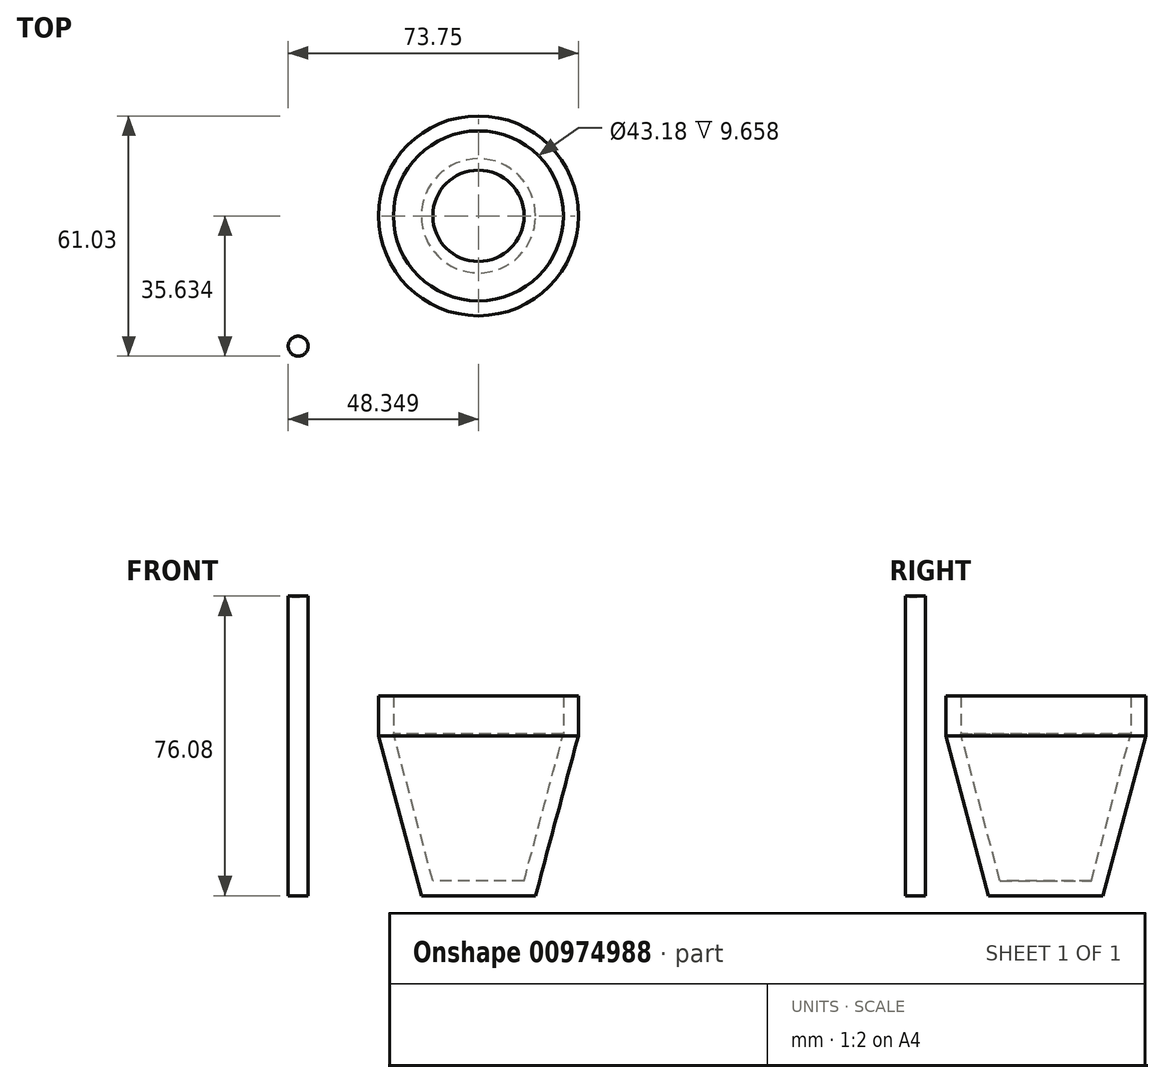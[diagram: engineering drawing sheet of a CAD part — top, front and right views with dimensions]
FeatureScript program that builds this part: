
annotation { "Feature Type Name" : "Feature", "Feature Type Description" : "" }
export const myFeature = defineFeature(function(context is Context, id is Id, definition is map)
    precondition{}
    {
        {
            var Q0;
            Q0=qCreatedBy(makeId("Top.planeOp"),FACE);
            var sketch = newSketch(context, id + "F0", { "sketchPlane" : qUnion([Q0])});
            skCircle(sketch, "E0", {"center": v(0, 0) * mm, "radius": 2.54 * mm});
            skSolve(sketch);
        }
        {
            var Q0;
            Q0 = qSketchRegion(id + "F0", true);
            extrude(context, id + "F1", {"entities" : qUnion([Q0]), "depth" : 76.2 * mm, "offsetDistance" : 25.4 * mm});
        }
        {
            var Q0;
            Q0=qCreatedBy(makeId("Right.planeOp"),FACE);
            var sketch = newSketch(context, id + "F2", { "sketchPlane" : qUnion([Q0])});
            skLineSegment(sketch, "E1", {"start": v(0, 75.9) * mm, "end": v(0, 101.3) * mm});
            skArc(sketch, "E2", {"start": v(0, 101.3) * mm, "mid": v(-13.08, 88.6) * mm, "end": v(0, 75.9) * mm});
            skSolve(sketch);
        }
        {
            var Q0;
            Q0=makeQuery(id+"F2.imprint","IMPRINT",FACE,{"disambiguationData":[TD([[makeQuery(id+"F2.imprint","IMPRINT",EDGE,{"derivedFrom":sQuery(id+"F2.wireOp",EDGE,"E1")}),1.0]])]});
            var Q1;
            Q1=sQuery(id+"F2.wireOp",EDGE,"E1");
            revolve(context, id + "F3", {"operationType" : NewBodyOperationType.ADD, "surfaceOperationType" : NewSurfaceOperationType.NEW, "entities" : qUnion([Q0]), "axis" : qUnion([Q1]), "revolveType" : RevolveType.FULL});
        }
        {
            var Q0;
            Q0=qCreatedBy(makeId("Top.planeOp"),FACE);
            var sketch = newSketch(context, id + "F4", { "sketchPlane" : qUnion([Q0])});
            skCircle(sketch, "E3", {"center": v(45.8, 33.1) * mm, "radius": 25.4 * mm});
            skSolve(sketch);
        }
        {
            var Q0;
            Q0 = qSketchRegion(id + "F4", true);
            extrude(context, id + "F5", {"entities" : qUnion([Q0]), "depth" : 50.8 * mm, "offsetDistance" : 25.4 * mm});
        }
        {
            var Q0;
            Q0=makeQuery(id+"F5.opExtrude","CAP_EDGE",EDGE,{"disambiguationData":[OSD([sQuery(id+"F4.wireOp",EDGE,"E3")])],"isStart":true});
            chamfer(context, id + "F6", {"entities" : qUnion([Q0]), "chamferType" : ChamferType.OFFSET_ANGLE, "width" : 40.64 * mm, "oppositeDirection" : false, "angle" : 15 * degree});
        }
        {
            var Q0;
            Q0=makeQuery(id+"F5.opExtrude","CAP_FACE",FACE,{"disambiguationData":[OSD([sQuery(id+"F4.wireOp",EDGE,"E3")])],"isStart":false});
            shell(context, id + "F7", {"entities" : qUnion([Q0]), "thickness" : 3.8 * mm});
        }
    });
